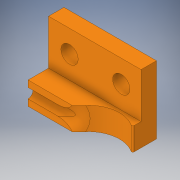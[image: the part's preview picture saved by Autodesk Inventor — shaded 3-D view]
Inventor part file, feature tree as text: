
AUTODESK INVENTOR PART (.ipt)
format: ipt  version: 2017 (Build 210142000, 142)  size: 178,176 bytes
history: native  units: in
note: dims shown in document units (in); Inventor stores cm internally (conversion verified against a paired STEP export)
features: extrude x5, sketch x5, fillet x2
ambient origin geometry x8: Origin, YZ Plane, XZ Plane, XY Plane, X Axis, Y Axis, Z Axis, Center Point
bodies: Solid1 (feature_tree)
feature tree (12):
  extrude  "Extrusion1"  Depth=0.55in
  extrude  "Extrusion2"  Depth=0.75in
  extrude  "Extrusion3"  Depth=1.0in TaperAngle=0.0deg
  extrude  "Extrusion4"  Depth=0.15in
  fillet  "Fillet1"  Radius=0.5in
  fillet  "Fillet2"  Radius=1.0in
  extrude  "Extrusion5"  Depth=0.01in TaperAngle=0.0deg
  sketch  "Sketch1"  dims[d0=0.75in d1=0.55in]
  sketch  "Sketch2"  dims[d2=0.125in d3=0.0in d4=0.75in]
  sketch  "Sketch3"  dims[d5=0.365in d6=1.0in d7=0.0in]
  sketch  "Sketch4"  dims[d8=0.4in d9=0.15in d10=0.5in d11=1.0in d12=0.0in]
  sketch  "Sketch5"  dims[d13=0.08in d14=1.0in d15=0.0in d16=0.125in d17=0.01in d18=0.14in d19=0.14in d20=0.16in d21=0.58in d22=1.0in d23=0.0in]
